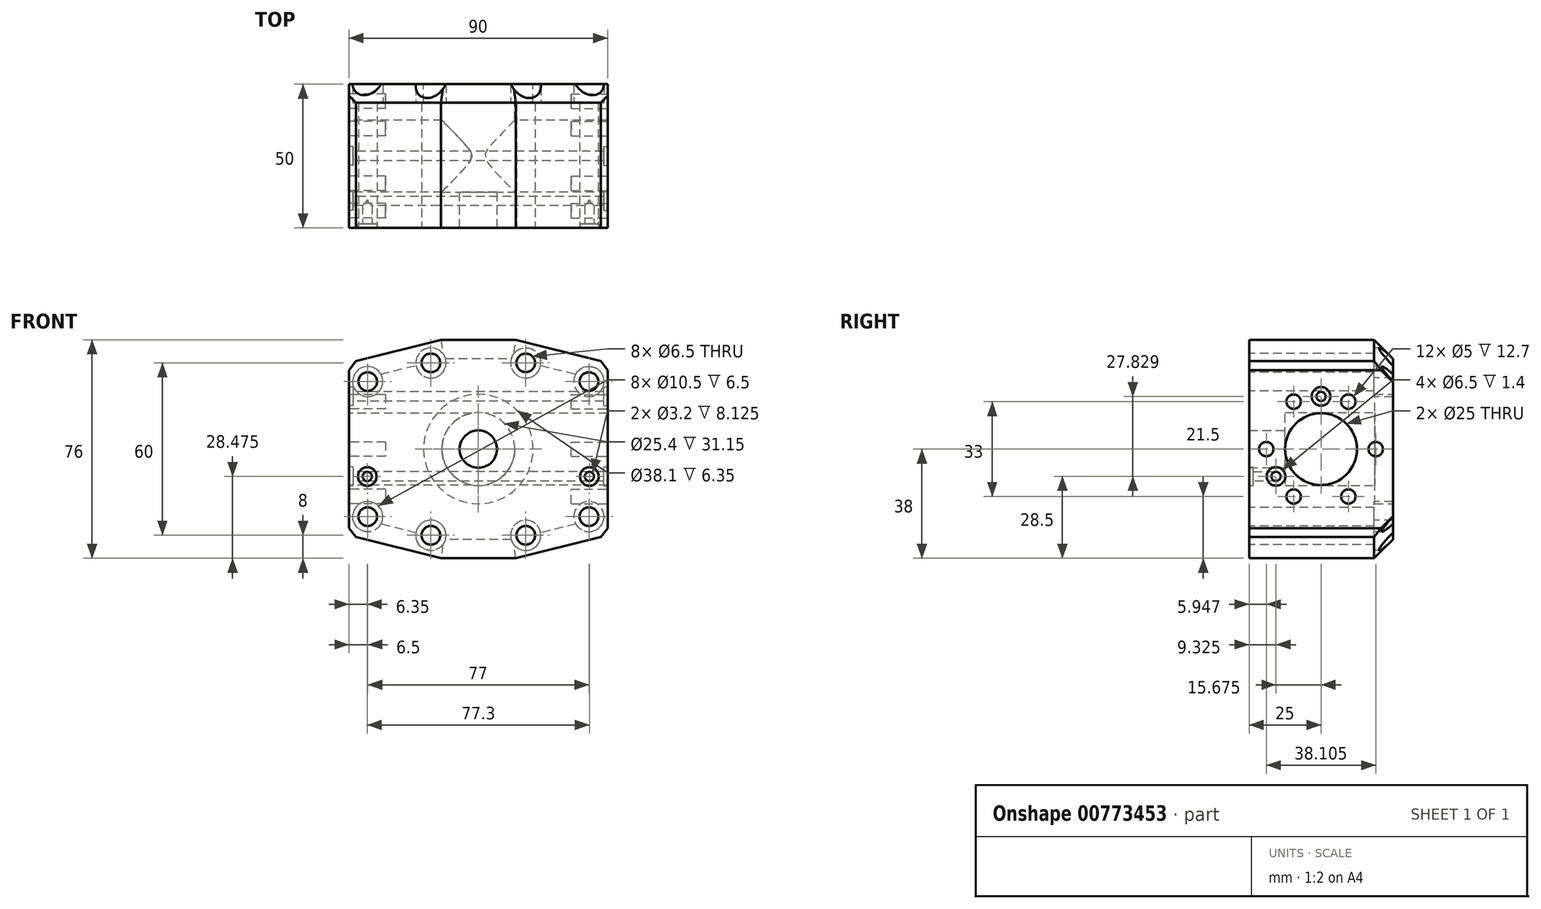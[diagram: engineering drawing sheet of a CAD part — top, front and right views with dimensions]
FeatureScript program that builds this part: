
annotation { "Feature Type Name" : "Feature", "Feature Type Description" : "" }
export const myFeature = defineFeature(function(context is Context, id is Id, definition is map)
    precondition{}
    {
        {
            var Q0;
            Q0=qCreatedBy(makeId("Front.planeOp"),FACE);
            var sketch = newSketch(context, id + "F0", { "sketchPlane" : qUnion([Q0])});
            skLineSegment(sketch, "E0.bottom", {"start": v(-45, 30) * mm, "end": v(45, 30) * mm});
            skLineSegment(sketch, "E0.top", {"start": v(-45, -30) * mm, "end": v(45, -30) * mm});
            skLineSegment(sketch, "E0.left", {"start": v(-45, 30) * mm, "end": v(-45, -30) * mm});
            skLineSegment(sketch, "E0.right", {"start": v(45, 30) * mm, "end": v(45, -30) * mm});
            skPoint(sketch, "E0.middle", {"position": v(0, 0) * mm});
            skPoint(sketch, "E1", {"position": v(0, 38) * mm});
            skLineSegment(sketch, "E2", {"start": v(0, 38) * mm, "end": v(-13, 38) * mm});
            skLineSegment(sketch, "E3", {"start": v(0, 38) * mm, "end": v(13, 38) * mm});
            skLineSegment(sketch, "E4", {"start": v(13, 38) * mm, "end": v(45, 30) * mm});
            skLineSegment(sketch, "E5", {"start": v(-13, 38) * mm, "end": v(-45, 30) * mm});
            skPoint(sketch, "E6", {"position": v(0, -38) * mm});
            skLineSegment(sketch, "E7", {"start": v(0, -38) * mm, "end": v(-13, -38) * mm});
            skLineSegment(sketch, "E8", {"start": v(-13, -38) * mm, "end": v(0, -38) * mm});
            skLineSegment(sketch, "E9", {"start": v(-13, -38) * mm, "end": v(-45, -30) * mm});
            skLineSegment(sketch, "E10", {"start": v(0, -38) * mm, "end": v(13, -38) * mm});
            skLineSegment(sketch, "E11", {"start": v(13, -38) * mm, "end": v(45, -30) * mm});
            skCircle(sketch, "E12", {"center": v(0, 0) * mm, "radius": 6.5 * mm});
            skPoint(sketch, "E13", {"position": v(-38.5, 23.5) * mm});
            skPoint(sketch, "E14", {"position": v(38.5, 23.5) * mm});
            skPoint(sketch, "E15", {"position": v(38.5, -23.5) * mm});
            skPoint(sketch, "E16", {"position": v(-38.5, -23.5) * mm});
            skPoint(sketch, "E17", {"position": v(-16.5, 30) * mm});
            skPoint(sketch, "E18", {"position": v(16.5, 30) * mm});
            skPoint(sketch, "E19", {"position": v(-16.5, -30) * mm});
            skPoint(sketch, "E20", {"position": v(16.5, -30) * mm});
            skSolve(sketch);
        }
        {
            var Q0;
            Q0 = qSketchRegion(id + "F0", true);
            extrude(context, id + "F1", {"entities" : qUnion([Q0]), "depth" : 50 * mm, "offsetDistance" : 25.4 * mm});
        }
        {
            var Q0;
            Q0=sQuery(id+"F0.wireOp",VERTEX,"E13");
            var Q1;
            Q1=sQuery(id+"F0.wireOp",VERTEX,"E17");
            var Q2;
            Q2=sQuery(id+"F0.wireOp",VERTEX,"E18");
            var Q3;
            Q3=sQuery(id+"F0.wireOp",VERTEX,"E14");
            var Q4;
            Q4=sQuery(id+"F0.wireOp",VERTEX,"E15");
            var Q5;
            Q5=sQuery(id+"F0.wireOp",VERTEX,"E20");
            var Q6;
            Q6=sQuery(id+"F0.wireOp",VERTEX,"E19");
            var Q7;
            Q7=sQuery(id+"F0.wireOp",VERTEX,"E16");
            var Q8;
            Q8=makeQuery(id+"F1.opExtrude","SWEPT_BODY",BODY,{"disambiguationData":[OSD([sQuery(id+"F0.wireOp",EDGE,"E0.left"),sQuery(id+"F0.wireOp",EDGE,"E0.right"),sQuery(id+"F0.wireOp",EDGE,"E2"),sQuery(id+"F0.wireOp",EDGE,"E3"),sQuery(id+"F0.wireOp",EDGE,"E4"),sQuery(id+"F0.wireOp",EDGE,"E5"),sQuery(id+"F0.wireOp",EDGE,"E8"),sQuery(id+"F0.wireOp",EDGE,"E9"),sQuery(id+"F0.wireOp",EDGE,"E10"),sQuery(id+"F0.wireOp",EDGE,"E11"),sQuery(id+"F0.wireOp",EDGE,"E12")])]});
            hole(context, id + "F2", {"style" : HoleStyle.C_BORE, "endStyle" : HoleEndStyle.THROUGH, "oppositeDirection" : true, "holeDiameter" : 6.5 * mm, "cBoreDiameter" : 10.5 * mm, "cBoreDepth" : 6.5 * mm, "majorDiameter" : 6.35 * mm, "isTappedThrough" : true, "tappedDepth" : 12.7 * mm, "tapClearance" : 3, "locations" : qUnion([Q0, Q1, Q2, Q3, Q4, Q5, Q6, Q7]), "scope" : qUnion([Q8])});
        }
        {
            var Q0;
            Q0=makeQuery(id+"F1.opExtrude","CAP_EDGE",EDGE,{"disambiguationData":[OSD([sQuery(id+"F0.wireOp",EDGE,"E4")])],"isStart":true});
            var Q1;
            Q1=makeQuery(id+"F1.opExtrude","CAP_EDGE",EDGE,{"disambiguationData":[OSD([sQuery(id+"F0.wireOp",EDGE,"E2"),sQuery(id+"F0.wireOp",EDGE,"E3")])],"isStart":true});
            var Q2;
            Q2=makeQuery(id+"F1.opExtrude","CAP_EDGE",EDGE,{"disambiguationData":[OSD([sQuery(id+"F0.wireOp",EDGE,"E5")])],"isStart":true});
            var Q3;
            Q3=makeQuery(id+"F1.opExtrude","CAP_EDGE",EDGE,{"disambiguationData":[OSD([sQuery(id+"F0.wireOp",EDGE,"E9")])],"isStart":true});
            var Q4;
            Q4=makeQuery(id+"F1.opExtrude","CAP_EDGE",EDGE,{"disambiguationData":[OSD([sQuery(id+"F0.wireOp",EDGE,"E8"),sQuery(id+"F0.wireOp",EDGE,"E10")])],"isStart":true});
            var Q5;
            Q5=makeQuery(id+"F1.opExtrude","CAP_EDGE",EDGE,{"disambiguationData":[OSD([sQuery(id+"F0.wireOp",EDGE,"E11")])],"isStart":true});
            chamfer(context, id + "F3", {"entities" : qUnion([Q0, Q1, Q2, Q3, Q4, Q5]), "width" : 6.5 * mm, "tangentPropagation" : true});
        }
        {
            var Q0;
            Q0=makeQuery(id+"F0.imprint","IMPRINT",FACE,{"disambiguationData":[TD([[makeQuery(id+"F0.imprint","IMPRINT",EDGE,{"derivedFrom":sQuery(id+"F0.wireOp",EDGE,"E0.bottom")}),-1.0]])]});
            var sketch = newSketch(context, id + "F4", { "sketchPlane" : qUnion([Q0])});
            skCircle(sketch, "E21", {"center": v(0, 0) * mm, "radius": 12.7 * mm});
            skSolve(sketch);
        }
        {
            var Q0;
            Q0 = qSketchRegion(id + "F4", true);
            extrude(context, id + "F5", {"entities" : qUnion([Q0]), "operationType" : NewBodyOperationType.REMOVE, "depth" : 37.5 * mm, "offsetDistance" : 25.4 * mm});
        }
        {
            var Q0;
            Q0=makeQuery(id+"F1.opExtrude","SWEPT_FACE",FACE,{"disambiguationData":[OSD([sQuery(id+"F0.wireOp",EDGE,"E0.left")])]});
            var sketch = newSketch(context, id + "F6", { "sketchPlane" : qUnion([Q0])});
            skPoint(sketch, "E22", {"position": v(50, 0) * mm});
            skPoint(sketch, "E23", {"position": v(25, 0) * mm});
            skCircle(sketch, "E24", {"center": v(25, 0) * mm, "radius": 12.5 * mm});
            skPoint(sketch, "E25", {"position": v(25, 12.5) * mm});
            skPoint(sketch, "E26", {"position": v(12.5, 0) * mm});
            skPoint(sketch, "E27", {"position": v(25, -12.5) * mm});
            skPoint(sketch, "E28", {"position": v(37.5, 0) * mm});
            skPoint(sketch, "E29", {"position": v(25, 16.5) * mm});
            skPoint(sketch, "E30", {"position": v(9.3, 0) * mm});
            skPoint(sketch, "E31", {"position": v(40.68, 0) * mm});
            skPoint(sketch, "E32", {"position": v(40.68, -9.5) * mm});
            skCircle(sketch, "E33", {"center": v(40.68, -9.5) * mm, "radius": 1.6 * mm});
            skCircle(sketch, "E34.cCircle", {"center": v(25, 0) * mm, "radius": 16.5 * mm, "construction": true});
            skLineSegment(sketch, "E34.0", {"start": v(15.47, 16.5) * mm, "end": v(34.53, 16.5) * mm});
            skLineSegment(sketch, "E34.1", {"start": v(34.53, 16.5) * mm, "end": v(44.05, 0) * mm});
            skLineSegment(sketch, "E34.2", {"start": v(44.05, 0) * mm, "end": v(34.53, -16.5) * mm});
            skLineSegment(sketch, "E34.3", {"start": v(34.53, -16.5) * mm, "end": v(15.47, -16.5) * mm});
            skLineSegment(sketch, "E34.4", {"start": v(15.47, -16.5) * mm, "end": v(5.95, 0) * mm});
            skLineSegment(sketch, "E34.5", {"start": v(5.95, 0) * mm, "end": v(15.47, 16.5) * mm});
            skCircle(sketch, "E35", {"center": v(44.05, 0) * mm, "radius": 2.5 * mm});
            skCircle(sketch, "E36", {"center": v(34.53, -16.5) * mm, "radius": 2.5 * mm});
            skCircle(sketch, "E37", {"center": v(15.47, -16.5) * mm, "radius": 2.5 * mm});
            skCircle(sketch, "E38", {"center": v(5.95, 0) * mm, "radius": 2.5 * mm});
            skCircle(sketch, "E39", {"center": v(15.47, 16.5) * mm, "radius": 2.5 * mm});
            skCircle(sketch, "E40", {"center": v(34.53, 16.5) * mm, "radius": 2.5 * mm});
            skCircle(sketch, "E41", {"center": v(40.68, -9.5) * mm, "radius": 3.25 * mm});
            skPoint(sketch, "E42", {"position": v(25, 18.33) * mm});
            skCircle(sketch, "E43", {"center": v(25, 18.33) * mm, "radius": 1.6 * mm});
            skCircle(sketch, "E44", {"center": v(25, 18.33) * mm, "radius": 3.25 * mm});
            skSolve(sketch);
        }
        {
            var Q0;
            Q0=makeQuery(id+"F6.imprint","IMPRINT",FACE,{"disambiguationData":[TD([[makeQuery(id+"F6.imprint","IMPRINT",EDGE,{"derivedFrom":sQuery(id+"F6.wireOp",EDGE,"E24")}),1.0]])]});
            extrude(context, id + "F7", {"entities" : qUnion([Q0]), "operationType" : NewBodyOperationType.REMOVE, "endBound" : BoundingType.THROUGH_ALL, "oppositeDirection" : true, "depth" : 25.4 * mm, "offsetDistance" : 25.4 * mm});
        }
        {
            var Q0;
            Q0=makeQuery(id+"F6.imprint","IMPRINT",FACE,{"disambiguationData":[TD([[makeQuery(id+"F6.imprint","IMPRINT",EDGE,{"derivedFrom":sQuery(id+"F6.wireOp",EDGE,"QTD7NNXz-HLmn-tDvU-26fR-thVeX5AUPllZ")}),1.0]])]});
            var Q1;
            Q1=makeQuery(id+"F6.imprint","IMPRINT",FACE,{"disambiguationData":[TD([[makeQuery(id+"F6.imprint","IMPRINT",EDGE,{"derivedFrom":sQuery(id+"F6.wireOp",EDGE,"E33")}),1.0]])]});
            extrude(context, id + "F8", {"entities" : qUnion([Q0, Q1]), "operationType" : NewBodyOperationType.REMOVE, "oppositeDirection" : true, "depth" : 12.7 * mm, "offsetDistance" : 25.4 * mm});
        }
        {
            var Q0;
            Q0=makeQuery(id+"F1.opExtrude","SWEPT_FACE",FACE,{"disambiguationData":[OSD([sQuery(id+"F0.wireOp",EDGE,"E0.right")])]});
            var sketch = newSketch(context, id + "F9", { "sketchPlane" : qUnion([Q0])});
            skPoint(sketch, "E45", {"position": v(-25, 0) * mm});
            skPoint(sketch, "E46", {"position": v(-25, 12.5) * mm});
            skPoint(sketch, "E47", {"position": v(-12.5, 0) * mm});
            skPoint(sketch, "E48", {"position": v(-25, -12.5) * mm});
            skPoint(sketch, "E49", {"position": v(-37.5, 0) * mm});
            skCircle(sketch, "E50.cCircle", {"center": v(-25, 0) * mm, "radius": 16.5 * mm, "construction": true});
            skLineSegment(sketch, "E50.0", {"start": v(-34.53, 16.5) * mm, "end": v(-15.47, 16.5) * mm});
            skLineSegment(sketch, "E50.1", {"start": v(-15.47, 16.5) * mm, "end": v(-5.95, 0) * mm});
            skLineSegment(sketch, "E50.2", {"start": v(-5.95, 0) * mm, "end": v(-15.47, -16.5) * mm});
            skLineSegment(sketch, "E50.3", {"start": v(-15.47, -16.5) * mm, "end": v(-34.53, -16.5) * mm});
            skLineSegment(sketch, "E50.4", {"start": v(-34.53, -16.5) * mm, "end": v(-44.05, 0) * mm});
            skLineSegment(sketch, "E50.5", {"start": v(-44.05, 0) * mm, "end": v(-34.53, 16.5) * mm});
            skPoint(sketch, "E50.0.midPoint", {"position": v(-25, 16.5) * mm});
            skCircle(sketch, "E51", {"center": v(-34.53, 16.5) * mm, "radius": 2.5 * mm});
            skCircle(sketch, "E52", {"center": v(-15.47, 16.5) * mm, "radius": 2.5 * mm});
            skCircle(sketch, "E53", {"center": v(-5.95, 0) * mm, "radius": 2.5 * mm});
            skCircle(sketch, "E54", {"center": v(-15.47, -16.5) * mm, "radius": 2.5 * mm});
            skCircle(sketch, "E55", {"center": v(-34.53, -16.5) * mm, "radius": 2.5 * mm});
            skCircle(sketch, "E56", {"center": v(-44.05, 0) * mm, "radius": 2.5 * mm});
            skPoint(sketch, "E57", {"position": v(-25, 18.33) * mm});
            skPoint(sketch, "E58", {"position": v(-40.67, -9.5) * mm});
            skCircle(sketch, "E59", {"center": v(-40.67, -9.5) * mm, "radius": 3.25 * mm});
            skCircle(sketch, "E60", {"center": v(-25, 18.33) * mm, "radius": 3.25 * mm});
            skSolve(sketch);
        }
        {
            var Q0;
            {var subQ0=sQuery(id+"F9.wireOp",EDGE,"E50.5");var subQ1=sQuery(id+"F9.wireOp",EDGE,"E50.4");var subQ2=makeQuery(id+"F9.imprint","INTERSECT",VERTEX,{"derivedFrom":[subQ1,subQ0]});Q0=makeQuery(id+"F9.imprint","IMPRINT",FACE,{"disambiguationData":[TD([[makeQuery(id+"F9.imprint","IMPRINT",EDGE,{"disambiguationData":[TD([[subQ2,1.0]])],"derivedFrom":subQ1}),-1.0]])]});}
            var Q1;
            {var subQ0=sQuery(id+"F9.wireOp",EDGE,"E50.5");var subQ1=sQuery(id+"F9.wireOp",EDGE,"E50.4");var subQ2=makeQuery(id+"F9.imprint","INTERSECT",VERTEX,{"derivedFrom":[subQ1,subQ0]});Q1=makeQuery(id+"F9.imprint","IMPRINT",FACE,{"disambiguationData":[TD([[makeQuery(id+"F9.imprint","IMPRINT",EDGE,{"disambiguationData":[TD([[subQ2,1.0]])],"derivedFrom":subQ1}),1.0]])]});}
            var Q2;
            {var subQ0=sQuery(id+"F9.wireOp",EDGE,"E50.4");var subQ1=sQuery(id+"F9.wireOp",EDGE,"E50.3");var subQ2=makeQuery(id+"F9.imprint","INTERSECT",VERTEX,{"derivedFrom":[subQ1,subQ0]});Q2=makeQuery(id+"F9.imprint","IMPRINT",FACE,{"disambiguationData":[TD([[makeQuery(id+"F9.imprint","IMPRINT",EDGE,{"disambiguationData":[TD([[subQ2,1.0]])],"derivedFrom":subQ1}),1.0]])]});}
            var Q3;
            {var subQ0=sQuery(id+"F9.wireOp",EDGE,"E50.4");var subQ1=sQuery(id+"F9.wireOp",EDGE,"E50.3");var subQ2=makeQuery(id+"F9.imprint","INTERSECT",VERTEX,{"derivedFrom":[subQ1,subQ0]});Q3=makeQuery(id+"F9.imprint","IMPRINT",FACE,{"disambiguationData":[TD([[makeQuery(id+"F9.imprint","IMPRINT",EDGE,{"disambiguationData":[TD([[subQ2,1.0]])],"derivedFrom":subQ1}),-1.0]])]});}
            var Q4;
            {var subQ0=sQuery(id+"F9.wireOp",EDGE,"E50.3");var subQ1=sQuery(id+"F9.wireOp",EDGE,"E50.2");var subQ2=makeQuery(id+"F9.imprint","INTERSECT",VERTEX,{"derivedFrom":[subQ1,subQ0]});Q4=makeQuery(id+"F9.imprint","IMPRINT",FACE,{"disambiguationData":[TD([[makeQuery(id+"F9.imprint","IMPRINT",EDGE,{"disambiguationData":[TD([[subQ2,1.0]])],"derivedFrom":subQ1}),1.0]])]});}
            var Q5;
            {var subQ0=sQuery(id+"F9.wireOp",EDGE,"E50.3");var subQ1=sQuery(id+"F9.wireOp",EDGE,"E50.2");var subQ2=makeQuery(id+"F9.imprint","INTERSECT",VERTEX,{"derivedFrom":[subQ1,subQ0]});Q5=makeQuery(id+"F9.imprint","IMPRINT",FACE,{"disambiguationData":[TD([[makeQuery(id+"F9.imprint","IMPRINT",EDGE,{"disambiguationData":[TD([[subQ2,1.0]])],"derivedFrom":subQ1}),-1.0]])]});}
            var Q6;
            {var subQ0=sQuery(id+"F9.wireOp",EDGE,"E50.2");var subQ1=sQuery(id+"F9.wireOp",EDGE,"E50.1");var subQ2=makeQuery(id+"F9.imprint","INTERSECT",VERTEX,{"derivedFrom":[subQ1,subQ0]});Q6=makeQuery(id+"F9.imprint","IMPRINT",FACE,{"disambiguationData":[TD([[makeQuery(id+"F9.imprint","IMPRINT",EDGE,{"disambiguationData":[TD([[subQ2,1.0]])],"derivedFrom":subQ1}),1.0]])]});}
            var Q7;
            {var subQ0=sQuery(id+"F9.wireOp",EDGE,"E50.2");var subQ1=sQuery(id+"F9.wireOp",EDGE,"E50.1");var subQ2=makeQuery(id+"F9.imprint","INTERSECT",VERTEX,{"derivedFrom":[subQ1,subQ0]});Q7=makeQuery(id+"F9.imprint","IMPRINT",FACE,{"disambiguationData":[TD([[makeQuery(id+"F9.imprint","IMPRINT",EDGE,{"disambiguationData":[TD([[subQ2,1.0]])],"derivedFrom":subQ1}),-1.0]])]});}
            var Q8;
            {var subQ0=sQuery(id+"F9.wireOp",EDGE,"E50.5");var subQ1=sQuery(id+"F9.wireOp",EDGE,"E50.0");var subQ2=makeQuery(id+"F9.imprint","INTERSECT",VERTEX,{"derivedFrom":[subQ1,subQ0]});Q8=makeQuery(id+"F9.imprint","IMPRINT",FACE,{"disambiguationData":[TD([[makeQuery(id+"F9.imprint","IMPRINT",EDGE,{"disambiguationData":[TD([[subQ2,-1.0]])],"derivedFrom":subQ1}),-1.0]])]});}
            var Q9;
            {var subQ0=sQuery(id+"F9.wireOp",EDGE,"E50.5");var subQ1=sQuery(id+"F9.wireOp",EDGE,"E50.0");var subQ2=makeQuery(id+"F9.imprint","INTERSECT",VERTEX,{"derivedFrom":[subQ1,subQ0]});Q9=makeQuery(id+"F9.imprint","IMPRINT",FACE,{"disambiguationData":[TD([[makeQuery(id+"F9.imprint","IMPRINT",EDGE,{"disambiguationData":[TD([[subQ2,-1.0]])],"derivedFrom":subQ1}),1.0]])]});}
            var Q10;
            {var subQ0=sQuery(id+"F9.wireOp",EDGE,"E50.1");var subQ1=sQuery(id+"F9.wireOp",EDGE,"E50.0");var subQ2=makeQuery(id+"F9.imprint","INTERSECT",VERTEX,{"derivedFrom":[subQ1,subQ0]});Q10=makeQuery(id+"F9.imprint","IMPRINT",FACE,{"disambiguationData":[TD([[makeQuery(id+"F9.imprint","IMPRINT",EDGE,{"disambiguationData":[TD([[subQ2,1.0]])],"derivedFrom":subQ1}),-1.0]])]});}
            var Q11;
            {var subQ0=sQuery(id+"F9.wireOp",EDGE,"E50.1");var subQ1=sQuery(id+"F9.wireOp",EDGE,"E50.0");var subQ2=makeQuery(id+"F9.imprint","INTERSECT",VERTEX,{"derivedFrom":[subQ1,subQ0]});Q11=makeQuery(id+"F9.imprint","IMPRINT",FACE,{"disambiguationData":[TD([[makeQuery(id+"F9.imprint","IMPRINT",EDGE,{"disambiguationData":[TD([[subQ2,1.0]])],"derivedFrom":subQ1}),1.0]])]});}
            extrude(context, id + "F10", {"entities" : qUnion([Q0, Q1, Q2, Q3, Q4, Q5, Q6, Q7, Q8, Q9, Q10, Q11]), "operationType" : NewBodyOperationType.REMOVE, "oppositeDirection" : true, "depth" : 12.7 * mm, "offsetDistance" : 25.4 * mm});
        }
        {
            var Q0;
            Q0=makeQuery(id+"F0.imprint","IMPRINT",FACE,{"disambiguationData":[TD([[makeQuery(id+"F0.imprint","IMPRINT",EDGE,{"derivedFrom":sQuery(id+"F0.wireOp",EDGE,"E0.bottom")}),-1.0]])]});
            var sketch = newSketch(context, id + "F11", { "sketchPlane" : qUnion([Q0])});
            skCircle(sketch, "E61", {"center": v(0, 0) * mm, "radius": 19.05 * mm});
            skSolve(sketch);
        }
        {
            var Q0;
            Q0=makeQuery(id+"F11.imprint","IMPRINT",FACE,{"disambiguationData":[TD([[makeQuery(id+"F11.imprint","IMPRINT",EDGE,{"derivedFrom":sQuery(id+"F11.wireOp",EDGE,"E61")}),1.0]])]});
            extrude(context, id + "F12", {"entities" : qUnion([Q0]), "operationType" : NewBodyOperationType.REMOVE, "depth" : 6.35 * mm, "offsetDistance" : 25.4 * mm});
        }
        {
            var Q0;
            Q0=makeQuery(id+"F1.opExtrude","SWEPT_EDGE",EDGE,{"disambiguationData":[OSD([sQuery(id+"F0.wireOp",EDGE,"E0.bottom"),sQuery(id+"F0.wireOp",EDGE,"E0.left"),sQuery(id+"F0.wireOp",EDGE,"E5")])]});
            var Q1;
            Q1=makeQuery(id+"F1.opExtrude","SWEPT_EDGE",EDGE,{"disambiguationData":[OSD([sQuery(id+"F0.wireOp",EDGE,"E0.bottom"),sQuery(id+"F0.wireOp",EDGE,"E0.right"),sQuery(id+"F0.wireOp",EDGE,"E4")])]});
            var Q2;
            Q2=makeQuery(id+"F1.opExtrude","SWEPT_EDGE",EDGE,{"disambiguationData":[OSD([sQuery(id+"F0.wireOp",EDGE,"E0.top"),sQuery(id+"F0.wireOp",EDGE,"E0.left"),sQuery(id+"F0.wireOp",EDGE,"E9")])]});
            var Q3;
            Q3=makeQuery(id+"F1.opExtrude","SWEPT_EDGE",EDGE,{"disambiguationData":[OSD([sQuery(id+"F0.wireOp",EDGE,"E0.top"),sQuery(id+"F0.wireOp",EDGE,"E0.right"),sQuery(id+"F0.wireOp",EDGE,"E11")])]});
            chamfer(context, id + "F13", {"entities" : qUnion([Q0, Q1, Q2, Q3]), "width" : 3.17 * mm, "tangentPropagation" : true});
        }
        {
            var Q0;
            Q0=makeQuery(id+"F8.boolean.opBoolean","COPY",FACE,{"derivedFrom":makeQuery(id+"F8.opExtrude","CAP_FACE",FACE,{"disambiguationData":[OSD([sQuery(id+"F6.wireOp",EDGE,"QTD7NNXz-HLmn-tDvU-26fR-thVeX5AUPllZ")])],"isStart":false})});
            var Q1;
            Q1=makeQuery(id+"F8.boolean.opBoolean","COPY",FACE,{"derivedFrom":makeQuery(id+"F8.opExtrude","CAP_FACE",FACE,{"disambiguationData":[OSD([sQuery(id+"F6.wireOp",EDGE,"E33")])],"isStart":false})});
            extrude(context, id + "F14", {"entities" : qUnion([Q0, Q1]), "operationType" : NewBodyOperationType.REMOVE, "endBound" : BoundingType.THROUGH_ALL, "oppositeDirection" : true, "depth" : 25.4 * mm, "offsetDistance" : 25.4 * mm});
        }
        {
            var Q0;
            Q0=makeQuery(id+"F1.opExtrude","CAP_FACE",FACE,{"disambiguationData":[OSD([sQuery(id+"F0.wireOp",EDGE,"E0.left"),sQuery(id+"F0.wireOp",EDGE,"E0.right"),sQuery(id+"F0.wireOp",EDGE,"E2"),sQuery(id+"F0.wireOp",EDGE,"E3"),sQuery(id+"F0.wireOp",EDGE,"E4"),sQuery(id+"F0.wireOp",EDGE,"E5"),sQuery(id+"F0.wireOp",EDGE,"E8"),sQuery(id+"F0.wireOp",EDGE,"E9"),sQuery(id+"F0.wireOp",EDGE,"E10"),sQuery(id+"F0.wireOp",EDGE,"E11"),sQuery(id+"F0.wireOp",EDGE,"E12")])],"isStart":false});
            var sketch = newSketch(context, id + "F15", { "sketchPlane" : qUnion([Q0])});
            skPoint(sketch, "E62", {"position": v(-38.65, -9.53) * mm});
            skCircle(sketch, "E63", {"center": v(-38.65, -9.53) * mm, "radius": 1.6 * mm});
            skPoint(sketch, "E64", {"position": v(38.65, -9.52) * mm});
            skCircle(sketch, "E65", {"center": v(38.65, -9.52) * mm, "radius": 1.6 * mm});
            skCircle(sketch, "E66", {"center": v(-38.65, -9.53) * mm, "radius": 3.25 * mm});
            skCircle(sketch, "E67", {"center": v(38.65, -9.52) * mm, "radius": 3.25 * mm});
            skSolve(sketch);
        }
        {
            var Q0;
            Q0=makeQuery(id+"F15.imprint","IMPRINT",FACE,{"disambiguationData":[TD([[makeQuery(id+"F15.imprint","IMPRINT",EDGE,{"derivedFrom":sQuery(id+"F15.wireOp",EDGE,"E63")}),1.0]])]});
            var Q1;
            Q1=makeQuery(id+"F15.imprint","IMPRINT",FACE,{"disambiguationData":[TD([[makeQuery(id+"F15.imprint","IMPRINT",EDGE,{"derivedFrom":sQuery(id+"F15.wireOp",EDGE,"E65")}),1.0]])]});
            extrude(context, id + "F16", {"entities" : qUnion([Q0, Q1]), "operationType" : NewBodyOperationType.REMOVE, "oppositeDirection" : true, "depth" : 9.52 * mm, "offsetDistance" : 25.4 * mm});
        }
        {
            var Q0;
            Q0=makeQuery(id+"F15.imprint","IMPRINT",FACE,{"disambiguationData":[TD([[makeQuery(id+"F15.imprint","IMPRINT",EDGE,{"derivedFrom":sQuery(id+"F15.wireOp",EDGE,"E63")}),-1.0]])]});
            var Q1;
            Q1=makeQuery(id+"F15.imprint","IMPRINT",FACE,{"disambiguationData":[TD([[makeQuery(id+"F15.imprint","IMPRINT",EDGE,{"derivedFrom":sQuery(id+"F15.wireOp",EDGE,"E65")}),-1.0]])]});
            extrude(context, id + "F17", {"entities" : qUnion([Q0, Q1]), "operationType" : NewBodyOperationType.REMOVE, "oppositeDirection" : true, "depth" : 1.4 * mm, "offsetDistance" : 25.4 * mm});
        }
        {
            var Q0;
            {var subQ0=sQuery(id+"F6.wireOp",EDGE,"E34.5");var subQ1=sQuery(id+"F6.wireOp",EDGE,"E34.0");var subQ2=makeQuery(id+"F6.imprint","INTERSECT",VERTEX,{"derivedFrom":[subQ1,subQ0]});Q0=makeQuery(id+"F6.imprint","IMPRINT",FACE,{"disambiguationData":[TD([[makeQuery(id+"F6.imprint","IMPRINT",EDGE,{"disambiguationData":[TD([[subQ2,-1.0]])],"derivedFrom":subQ1}),1.0]])]});}
            var Q1;
            {var subQ0=sQuery(id+"F6.wireOp",EDGE,"E34.5");var subQ1=sQuery(id+"F6.wireOp",EDGE,"E34.0");var subQ2=makeQuery(id+"F6.imprint","INTERSECT",VERTEX,{"derivedFrom":[subQ1,subQ0]});Q1=makeQuery(id+"F6.imprint","IMPRINT",FACE,{"disambiguationData":[TD([[makeQuery(id+"F6.imprint","IMPRINT",EDGE,{"disambiguationData":[TD([[subQ2,-1.0]])],"derivedFrom":subQ1}),-1.0]])]});}
            var Q2;
            {var subQ0=sQuery(id+"F6.wireOp",EDGE,"E34.1");var subQ1=sQuery(id+"F6.wireOp",EDGE,"E34.0");var subQ2=makeQuery(id+"F6.imprint","INTERSECT",VERTEX,{"derivedFrom":[subQ1,subQ0]});Q2=makeQuery(id+"F6.imprint","IMPRINT",FACE,{"disambiguationData":[TD([[makeQuery(id+"F6.imprint","IMPRINT",EDGE,{"disambiguationData":[TD([[subQ2,1.0]])],"derivedFrom":subQ1}),-1.0]])]});}
            var Q3;
            {var subQ0=sQuery(id+"F6.wireOp",EDGE,"E34.1");var subQ1=sQuery(id+"F6.wireOp",EDGE,"E34.0");var subQ2=makeQuery(id+"F6.imprint","INTERSECT",VERTEX,{"derivedFrom":[subQ1,subQ0]});Q3=makeQuery(id+"F6.imprint","IMPRINT",FACE,{"disambiguationData":[TD([[makeQuery(id+"F6.imprint","IMPRINT",EDGE,{"disambiguationData":[TD([[subQ2,1.0]])],"derivedFrom":subQ1}),1.0]])]});}
            var Q4;
            {var subQ0=sQuery(id+"F6.wireOp",EDGE,"E34.2");var subQ1=sQuery(id+"F6.wireOp",EDGE,"E34.1");var subQ2=makeQuery(id+"F6.imprint","INTERSECT",VERTEX,{"derivedFrom":[subQ1,subQ0]});Q4=makeQuery(id+"F6.imprint","IMPRINT",FACE,{"disambiguationData":[TD([[makeQuery(id+"F6.imprint","IMPRINT",EDGE,{"disambiguationData":[TD([[subQ2,1.0]])],"derivedFrom":subQ1}),1.0]])]});}
            var Q5;
            {var subQ0=sQuery(id+"F6.wireOp",EDGE,"E34.2");var subQ1=sQuery(id+"F6.wireOp",EDGE,"E34.1");var subQ2=makeQuery(id+"F6.imprint","INTERSECT",VERTEX,{"derivedFrom":[subQ1,subQ0]});Q5=makeQuery(id+"F6.imprint","IMPRINT",FACE,{"disambiguationData":[TD([[makeQuery(id+"F6.imprint","IMPRINT",EDGE,{"disambiguationData":[TD([[subQ2,1.0]])],"derivedFrom":subQ1}),-1.0]])]});}
            var Q6;
            {var subQ0=sQuery(id+"F6.wireOp",EDGE,"E34.3");var subQ1=sQuery(id+"F6.wireOp",EDGE,"E34.2");var subQ2=makeQuery(id+"F6.imprint","INTERSECT",VERTEX,{"derivedFrom":[subQ1,subQ0]});Q6=makeQuery(id+"F6.imprint","IMPRINT",FACE,{"disambiguationData":[TD([[makeQuery(id+"F6.imprint","IMPRINT",EDGE,{"disambiguationData":[TD([[subQ2,1.0]])],"derivedFrom":subQ1}),1.0]])]});}
            var Q7;
            {var subQ0=sQuery(id+"F6.wireOp",EDGE,"E34.3");var subQ1=sQuery(id+"F6.wireOp",EDGE,"E34.2");var subQ2=makeQuery(id+"F6.imprint","INTERSECT",VERTEX,{"derivedFrom":[subQ1,subQ0]});Q7=makeQuery(id+"F6.imprint","IMPRINT",FACE,{"disambiguationData":[TD([[makeQuery(id+"F6.imprint","IMPRINT",EDGE,{"disambiguationData":[TD([[subQ2,1.0]])],"derivedFrom":subQ1}),-1.0]])]});}
            var Q8;
            {var subQ0=sQuery(id+"F6.wireOp",EDGE,"E34.4");var subQ1=sQuery(id+"F6.wireOp",EDGE,"E34.3");var subQ2=makeQuery(id+"F6.imprint","INTERSECT",VERTEX,{"derivedFrom":[subQ1,subQ0]});Q8=makeQuery(id+"F6.imprint","IMPRINT",FACE,{"disambiguationData":[TD([[makeQuery(id+"F6.imprint","IMPRINT",EDGE,{"disambiguationData":[TD([[subQ2,1.0]])],"derivedFrom":subQ1}),1.0]])]});}
            var Q9;
            {var subQ0=sQuery(id+"F6.wireOp",EDGE,"E34.4");var subQ1=sQuery(id+"F6.wireOp",EDGE,"E34.3");var subQ2=makeQuery(id+"F6.imprint","INTERSECT",VERTEX,{"derivedFrom":[subQ1,subQ0]});Q9=makeQuery(id+"F6.imprint","IMPRINT",FACE,{"disambiguationData":[TD([[makeQuery(id+"F6.imprint","IMPRINT",EDGE,{"disambiguationData":[TD([[subQ2,1.0]])],"derivedFrom":subQ1}),-1.0]])]});}
            var Q10;
            {var subQ0=sQuery(id+"F6.wireOp",EDGE,"E34.5");var subQ1=sQuery(id+"F6.wireOp",EDGE,"E34.4");var subQ2=makeQuery(id+"F6.imprint","INTERSECT",VERTEX,{"derivedFrom":[subQ1,subQ0]});Q10=makeQuery(id+"F6.imprint","IMPRINT",FACE,{"disambiguationData":[TD([[makeQuery(id+"F6.imprint","IMPRINT",EDGE,{"disambiguationData":[TD([[subQ2,1.0]])],"derivedFrom":subQ1}),-1.0]])]});}
            var Q11;
            {var subQ0=sQuery(id+"F6.wireOp",EDGE,"E34.5");var subQ1=sQuery(id+"F6.wireOp",EDGE,"E34.4");var subQ2=makeQuery(id+"F6.imprint","INTERSECT",VERTEX,{"derivedFrom":[subQ1,subQ0]});Q11=makeQuery(id+"F6.imprint","IMPRINT",FACE,{"disambiguationData":[TD([[makeQuery(id+"F6.imprint","IMPRINT",EDGE,{"disambiguationData":[TD([[subQ2,1.0]])],"derivedFrom":subQ1}),1.0]])]});}
            extrude(context, id + "F18", {"entities" : qUnion([Q0, Q1, Q2, Q3, Q4, Q5, Q6, Q7, Q8, Q9, Q10, Q11]), "operationType" : NewBodyOperationType.REMOVE, "oppositeDirection" : true, "depth" : 12.7 * mm, "offsetDistance" : 25.4 * mm});
        }
        {
            var Q0;
            Q0=makeQuery(id+"F6.imprint","IMPRINT",FACE,{"disambiguationData":[TD([[makeQuery(id+"F6.imprint","IMPRINT",EDGE,{"derivedFrom":sQuery(id+"F6.wireOp",EDGE,"E33")}),-1.0]])]});
            var Q1;
            {var subQ0=sQuery(id+"F6.wireOp",EDGE,"E41");var subQ1=sQuery(id+"F6.wireOp",EDGE,"E34.2");var subQ2=makeQuery(id+"F6.imprint","INTERSECT",VERTEX,{"disambiguationData":[OD(0.0)],"derivedFrom":[subQ1,subQ0]});Q1=makeQuery(id+"F6.imprint","IMPRINT",FACE,{"disambiguationData":[TD([[makeQuery(id+"F6.imprint","IMPRINT",EDGE,{"disambiguationData":[TD([[subQ2,-1.0]])],"derivedFrom":subQ1}),-1.0]])]});}
            extrude(context, id + "F19", {"entities" : qUnion([Q0, Q1]), "operationType" : NewBodyOperationType.REMOVE, "oppositeDirection" : true, "depth" : 1.4 * mm, "offsetDistance" : 25 * mm});
        }
        {
            var Q0;
            Q0=makeQuery(id+"F6.imprint","IMPRINT",FACE,{"disambiguationData":[TD([[makeQuery(id+"F6.imprint","IMPRINT",EDGE,{"derivedFrom":sQuery(id+"F6.wireOp",EDGE,"E43")}),1.0]])]});
            extrude(context, id + "F20", {"entities" : qUnion([Q0]), "operationType" : NewBodyOperationType.REMOVE, "endBound" : BoundingType.THROUGH_ALL, "oppositeDirection" : true, "depth" : 25 * mm, "offsetDistance" : 25 * mm});
        }
        {
            var Q0;
            Q0=makeQuery(id+"F6.imprint","IMPRINT",FACE,{"disambiguationData":[TD([[makeQuery(id+"F6.imprint","IMPRINT",EDGE,{"derivedFrom":sQuery(id+"F6.wireOp",EDGE,"E43")}),-1.0]])]});
            var Q1;
            {var subQ0=sQuery(id+"F6.wireOp",EDGE,"E44");var subQ1=sQuery(id+"F6.wireOp",EDGE,"E34.0");var subQ2=makeQuery(id+"F6.imprint","INTERSECT",VERTEX,{"disambiguationData":[OD(0.0)],"derivedFrom":[subQ1,subQ0]});Q1=makeQuery(id+"F6.imprint","IMPRINT",FACE,{"disambiguationData":[TD([[makeQuery(id+"F6.imprint","IMPRINT",EDGE,{"disambiguationData":[TD([[subQ2,-1.0]])],"derivedFrom":subQ1}),-1.0]])]});}
            extrude(context, id + "F21", {"entities" : qUnion([Q0, Q1]), "operationType" : NewBodyOperationType.REMOVE, "oppositeDirection" : true, "depth" : 1.4 * mm, "offsetDistance" : 25 * mm});
        }
        {
            var Q0;
            {var subQ0=sQuery(id+"F9.wireOp",EDGE,"E59");var subQ1=sQuery(id+"F9.wireOp",EDGE,"E50.4");var subQ2=makeQuery(id+"F9.imprint","INTERSECT",VERTEX,{"disambiguationData":[OD(0.0)],"derivedFrom":[subQ1,subQ0]});Q0=makeQuery(id+"F9.imprint","IMPRINT",FACE,{"disambiguationData":[TD([[makeQuery(id+"F9.imprint","IMPRINT",EDGE,{"disambiguationData":[TD([[subQ2,-1.0]])],"derivedFrom":subQ1}),1.0]])]});}
            var Q1;
            {var subQ0=sQuery(id+"F9.wireOp",EDGE,"E59");var subQ1=sQuery(id+"F9.wireOp",EDGE,"E50.4");var subQ2=makeQuery(id+"F9.imprint","INTERSECT",VERTEX,{"disambiguationData":[OD(0.0)],"derivedFrom":[subQ1,subQ0]});Q1=makeQuery(id+"F9.imprint","IMPRINT",FACE,{"disambiguationData":[TD([[makeQuery(id+"F9.imprint","IMPRINT",EDGE,{"disambiguationData":[TD([[subQ2,-1.0]])],"derivedFrom":subQ1}),-1.0]])]});}
            var Q2;
            {var subQ0=sQuery(id+"F9.wireOp",EDGE,"E60");var subQ1=sQuery(id+"F9.wireOp",EDGE,"E50.0");var subQ2=makeQuery(id+"F9.imprint","INTERSECT",VERTEX,{"disambiguationData":[OD(0.0)],"derivedFrom":[subQ1,subQ0]});Q2=makeQuery(id+"F9.imprint","IMPRINT",FACE,{"disambiguationData":[TD([[makeQuery(id+"F9.imprint","IMPRINT",EDGE,{"disambiguationData":[TD([[subQ2,-1.0]])],"derivedFrom":subQ1}),1.0]])]});}
            var Q3;
            {var subQ0=sQuery(id+"F9.wireOp",EDGE,"E60");var subQ1=sQuery(id+"F9.wireOp",EDGE,"E50.0");var subQ2=makeQuery(id+"F9.imprint","INTERSECT",VERTEX,{"disambiguationData":[OD(0.0)],"derivedFrom":[subQ1,subQ0]});Q3=makeQuery(id+"F9.imprint","IMPRINT",FACE,{"disambiguationData":[TD([[makeQuery(id+"F9.imprint","IMPRINT",EDGE,{"disambiguationData":[TD([[subQ2,-1.0]])],"derivedFrom":subQ1}),-1.0]])]});}
            extrude(context, id + "F22", {"entities" : qUnion([Q0, Q1, Q2, Q3]), "operationType" : NewBodyOperationType.REMOVE, "oppositeDirection" : true, "depth" : 1.4 * mm, "offsetDistance" : 25 * mm});
        }
    });
